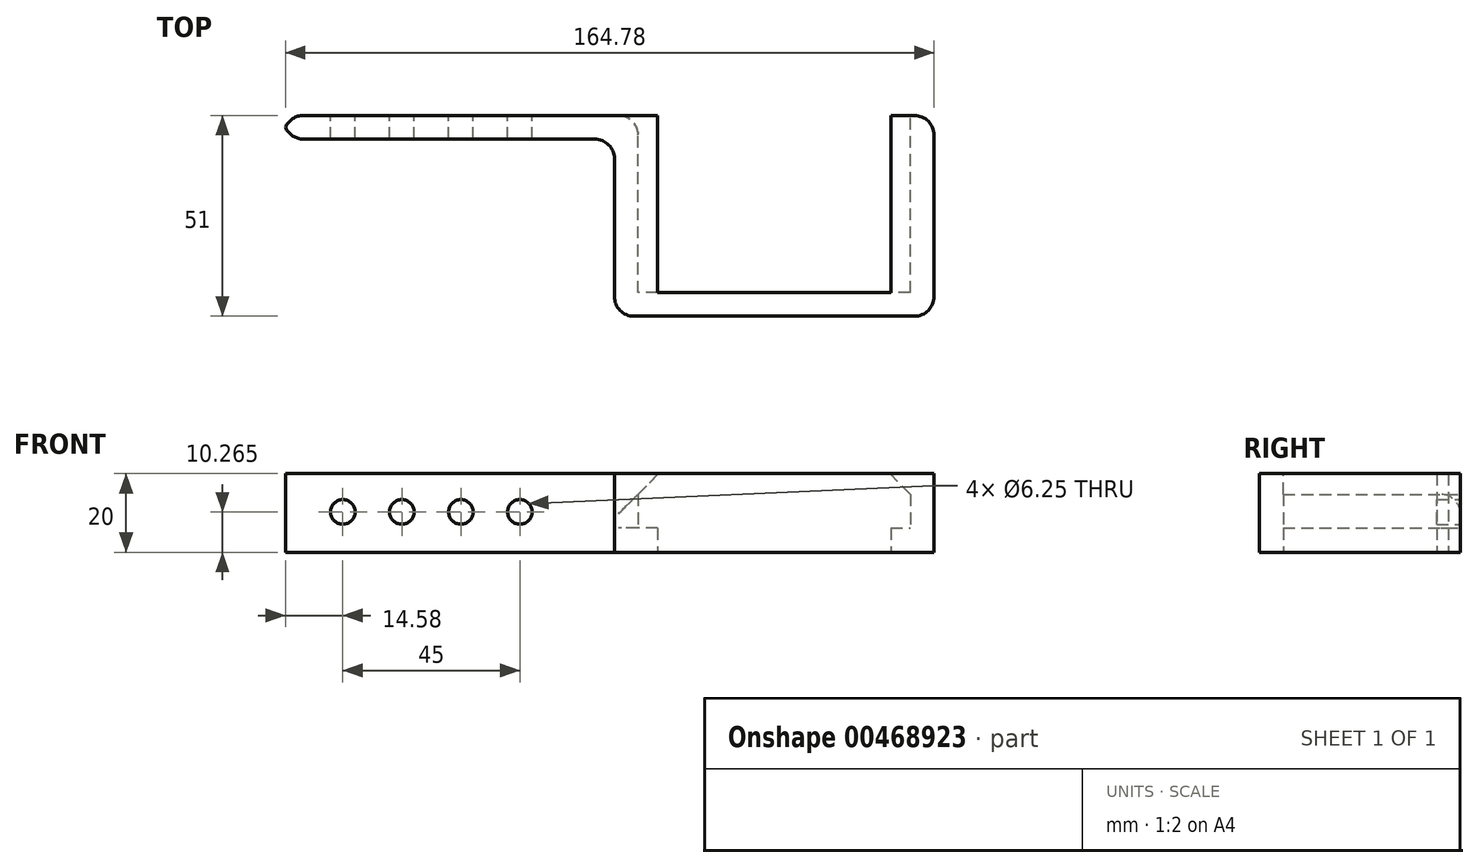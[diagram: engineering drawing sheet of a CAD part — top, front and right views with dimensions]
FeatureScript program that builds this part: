
annotation { "Feature Type Name" : "Feature", "Feature Type Description" : "" }
export const myFeature = defineFeature(function(context is Context, id is Id, definition is map)
    precondition{}
    {
        {
            var Q0;
            Q0=qCreatedBy(makeId("Top.planeOp"),FACE);
            var sketch = newSketch(context, id + "F0", { "sketchPlane" : qUnion([Q0])});
            skLineSegment(sketch, "E0", {"start": v(0, 0) * mm, "end": v(90, 0) * mm});
            skLineSegment(sketch, "E1", {"start": v(90, 0) * mm, "end": v(90, -45) * mm});
            skLineSegment(sketch, "E2", {"start": v(90, -45) * mm, "end": v(159.2, -45) * mm});
            skLineSegment(sketch, "E3", {"start": v(159.2, -45) * mm, "end": v(159.2, 0) * mm});
            skLineSegment(sketch, "E4", {"start": v(159.2, 0) * mm, "end": v(165.2, 0) * mm});
            skLineSegment(sketch, "E5", {"start": v(165.2, 0) * mm, "end": v(165.2, -45) * mm});
            skLineSegment(sketch, "E6", {"start": v(165.2, -45) * mm, "end": v(165.2, -51) * mm});
            skLineSegment(sketch, "E7", {"start": v(165.2, -51) * mm, "end": v(90, -51) * mm});
            skLineSegment(sketch, "E8", {"start": v(90, -51) * mm, "end": v(84, -51) * mm});
            skLineSegment(sketch, "E9", {"start": v(84, -51) * mm, "end": v(84, -6) * mm});
            skLineSegment(sketch, "E10", {"start": v(84, -6) * mm, "end": v(0, -6) * mm});
            skLineSegment(sketch, "E11", {"start": v(0, -6) * mm, "end": v(0, 0) * mm});
            skLineSegment(sketch, "E12", {"start": v(0, 0) * mm, "end": v(0, -6) * mm});
            skSolve(sketch);
        }
        {
            var Q0;
            Q0 = qSketchRegion(id + "F0", true);
            extrude(context, id + "F1", {"entities" : qUnion([Q0]), "depth" : 20 * mm});
        }
        {
            var Q0;
            Q0=makeQuery(id+"F1.opExtrude","SWEPT_FACE",FACE,{"disambiguationData":[OSD([sQuery(id+"F0.wireOp",EDGE,"E0")])]});
            var sketch = newSketch(context, id + "F2", { "sketchPlane" : qUnion([Q0])});
            skPoint(sketch, "E13", {"position": v(-15, 10.26) * mm});
            skPoint(sketch, "E14", {"position": v(-30, 10.26) * mm});
            skPoint(sketch, "E15", {"position": v(-45, 10.26) * mm});
            skPoint(sketch, "E16", {"position": v(-60, 10.26) * mm});
            skSolve(sketch);
        }
        {
            var Q0;
            Q0=sQuery(id+"F2.wireOp",VERTEX,"E15");
            var Q1;
            Q1=sQuery(id+"F2.wireOp",VERTEX,"E14");
            var Q2;
            Q2=sQuery(id+"F2.wireOp",VERTEX,"E13");
            var Q3;
            Q3=sQuery(id+"F2.wireOp",VERTEX,"E16");
            var Q4;
            Q4=makeQuery(id+"F1.opExtrude","SWEPT_BODY",BODY,{"disambiguationData":[OSD([sQuery(id+"F0.wireOp",EDGE,"E0"),sQuery(id+"F0.wireOp",EDGE,"E1"),sQuery(id+"F0.wireOp",EDGE,"E2"),sQuery(id+"F0.wireOp",EDGE,"E3"),sQuery(id+"F0.wireOp",EDGE,"E4"),sQuery(id+"F0.wireOp",EDGE,"E5"),sQuery(id+"F0.wireOp",EDGE,"E6"),sQuery(id+"F0.wireOp",EDGE,"E7"),sQuery(id+"F0.wireOp",EDGE,"E8"),sQuery(id+"F0.wireOp",EDGE,"E9"),sQuery(id+"F0.wireOp",EDGE,"E10"),sQuery(id+"F0.wireOp",EDGE,"E12")])]});
            hole(context, id + "F3", {"style" : HoleStyle.SIMPLE, "endStyle" : HoleEndStyle.THROUGH, "standardTappedOrClearance" : lookupTablePath({ "standard" : "ANSI", "size" : "D (0.25)", "type" : "Drilled" }), "standardBlindInLast" : lookupTablePath({ "standard" : "ANSI", "size" : "D", "type" : "Drilled" }), "holeDiameter" : 6.25 * mm, "isTappedThrough" : true, "tappedDepth" : 12 * mm, "tapClearance" : 3, "locations" : qUnion([Q0, Q1, Q2, Q3]), "scope" : qUnion([Q4])});
        }
        {
            var Q0;
            Q0=makeQuery(id+"F1.opExtrude","SWEPT_FACE",FACE,{"disambiguationData":[OSD([sQuery(id+"F0.wireOp",EDGE,"E3")])]});
            var sketch = newSketch(context, id + "F4", { "sketchPlane" : qUnion([Q0])});
            skPoint(sketch, "E17.startSnap0", {"position": v(45, 10) * mm});
            skLineSegment(sketch, "E18", {"start": v(51.78, 14.75) * mm, "end": v(0, 14.75) * mm});
            skLineSegment(sketch, "E19", {"start": v(51.46, 6.15) * mm, "end": v(0, 6.15) * mm});
            skSolve(sketch);
        }
        {
            var Q0;
            Q0=makeQuery(id+"F1.opExtrude","SWEPT_FACE",FACE,{"disambiguationData":[OSD([sQuery(id+"F0.wireOp",EDGE,"E1")])]});
            var sketch = newSketch(context, id + "F5", { "sketchPlane" : qUnion([Q0])});
            skLineSegment(sketch, "E20", {"start": v(-45, 14.75) * mm, "end": v(0, 14.75) * mm});
            skLineSegment(sketch, "E21", {"start": v(-45, 6.15) * mm, "end": v(0, 6.15) * mm});
            skSolve(sketch);
        }
        {
            var Q0;
            {var subQ1=sQuery(id+"F0.wireOp",EDGE,"E3");var subQ6=makeQuery(id+"F1.opExtrude","CAP_EDGE",EDGE,{"disambiguationData":[OSD([subQ1])],"isStart":true});Q0=makeQuery(id+"F4.imprint","IMPRINT",FACE,{"disambiguationData":[TD([[makeQuery(id+"F4.imprint","IMPRINT",EDGE,{"derivedFrom":subQ6}),-1.0]])]});}
            var Q1;
            {var subQ1=sQuery(id+"F0.wireOp",EDGE,"E3");var subQ6=makeQuery(id+"F1.opExtrude","CAP_EDGE",EDGE,{"disambiguationData":[OSD([subQ1])],"isStart":false});Q1=makeQuery(id+"F4.imprint","IMPRINT",FACE,{"disambiguationData":[TD([[makeQuery(id+"F4.imprint","IMPRINT",EDGE,{"derivedFrom":subQ6}),1.0]])]});}
            extrude(context, id + "F6", {"entities" : qUnion([Q0, Q1]), "operationType" : NewBodyOperationType.ADD, "depth" : 5 * mm});
        }
        {
            var Q0;
            {var subQ0=sQuery(id+"F5.wireOp",EDGE,"E21");Q0=makeQuery(id+"F5.imprint","IMPRINT",FACE,{"disambiguationData":[TD([[makeQuery(id+"F5.imprint","IMPRINT",EDGE,{"derivedFrom":subQ0}),-1.0]])]});}
            var Q1;
            {var subQ0=sQuery(id+"F5.wireOp",EDGE,"E20");Q1=makeQuery(id+"F5.imprint","IMPRINT",FACE,{"disambiguationData":[TD([[makeQuery(id+"F5.imprint","IMPRINT",EDGE,{"derivedFrom":subQ0}),1.0]])]});}
            extrude(context, id + "F7", {"entities" : qUnion([Q0, Q1]), "operationType" : NewBodyOperationType.ADD, "depth" : 5 * mm});
        }
        {
            var Q0;
            Q0=makeQuery(id+"F6.opExtrude","CAP_EDGE",EDGE,{"disambiguationData":[OSD([sQuery(id+"F4.wireOp",EDGE,"E18")])],"isStart":false});
            var Q1;
            Q1=makeQuery(id+"F7.opExtrude","CAP_EDGE",EDGE,{"disambiguationData":[OSD([sQuery(id+"F5.wireOp",EDGE,"E20")])],"isStart":false});
            chamfer(context, id + "F8", {"entities" : qUnion([Q0, Q1]), "width" : 5 * mm, "tangentPropagation" : true});
        }
        {
            var Q0;
            Q0=makeQuery(id+"F1.opExtrude","SWEPT_EDGE",EDGE,{"disambiguationData":[OSD([sQuery(id+"F0.wireOp",EDGE,"E6"),sQuery(id+"F0.wireOp",EDGE,"E7")])]});
            var Q1;
            Q1=makeQuery(id+"F1.opExtrude","SWEPT_EDGE",EDGE,{"disambiguationData":[OSD([sQuery(id+"F0.wireOp",EDGE,"E8"),sQuery(id+"F0.wireOp",EDGE,"E9")])]});
            var Q2;
            Q2=makeQuery(id+"F1.opExtrude","SWEPT_EDGE",EDGE,{"disambiguationData":[OSD([sQuery(id+"F0.wireOp",EDGE,"E0"),sQuery(id+"F0.wireOp",EDGE,"E12")])]});
            var Q3;
            Q3=makeQuery(id+"F1.opExtrude","SWEPT_EDGE",EDGE,{"disambiguationData":[OSD([sQuery(id+"F0.wireOp",EDGE,"E10"),sQuery(id+"F0.wireOp",EDGE,"E12")])]});
            fillet(context, id + "F9", {"entities" : qUnion([Q0, Q1, Q2, Q3]), "radius" : 5 * mm, "tangentPropagation" : true, "allowEdgeOverflow" : false});
        }
        {
            var Q0;
            Q0=makeQuery(id+"F1.opExtrude","SWEPT_EDGE",EDGE,{"disambiguationData":[OSD([sQuery(id+"F0.wireOp",EDGE,"E4"),sQuery(id+"F0.wireOp",EDGE,"E5")])]});
            fillet(context, id + "F10", {"entities" : qUnion([Q0]), "radius" : 5 * mm, "tangentPropagation" : true, "allowEdgeOverflow" : false});
        }
    });
